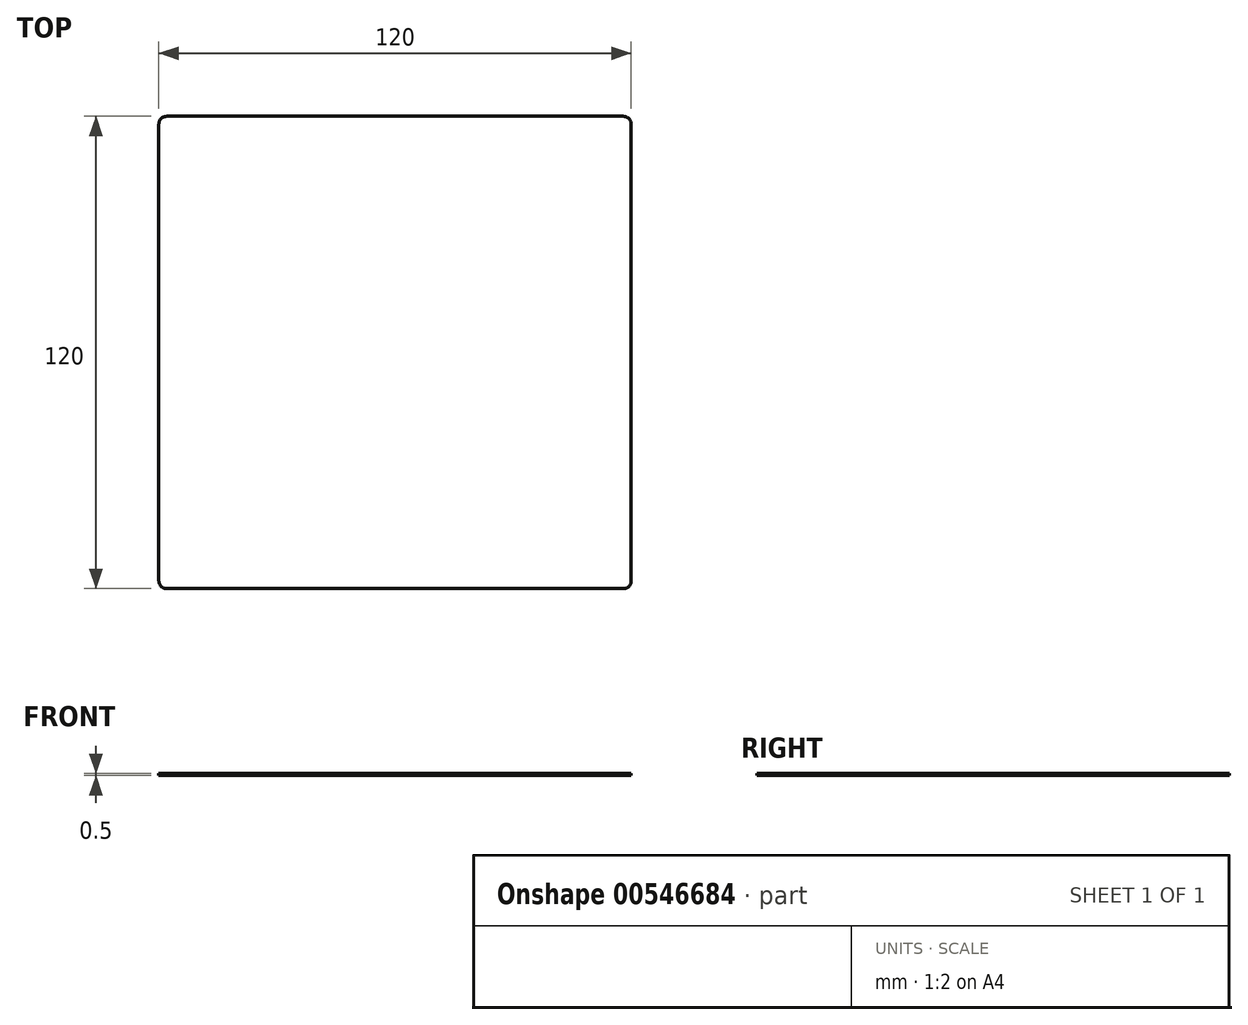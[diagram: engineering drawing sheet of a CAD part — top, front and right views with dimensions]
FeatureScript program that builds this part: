
annotation { "Feature Type Name" : "Feature", "Feature Type Description" : "" }
export const myFeature = defineFeature(function(context is Context, id is Id, definition is map)
    precondition{}
    {
        {
            var Q0;
            Q0=qCreatedBy(makeId("Top.planeOp"),FACE);
            var sketch = newSketch(context, id + "F0", { "sketchPlane" : qUnion([Q0])});
            skLineSegment(sketch, "E0.bottom", {"start": v(-60, -60) * mm, "end": v(60, -60) * mm});
            skLineSegment(sketch, "E0.top", {"start": v(-60, 60) * mm, "end": v(60, 60) * mm});
            skLineSegment(sketch, "E0.left", {"start": v(-60, -60) * mm, "end": v(-60, 60) * mm});
            skLineSegment(sketch, "E0.right", {"start": v(60, -60) * mm, "end": v(60, 60) * mm});
            skPoint(sketch, "E0.middle", {"position": v(0, 0) * mm});
            skSolve(sketch);
        }
        {
            var Q0;
            Q0 = qSketchRegion(id + "F0", true);
            extrude(context, id + "F1", {"entities" : qUnion([Q0]), "depth" : 0.5 * mm, "offsetDistance" : 25 * mm});
        }
        {
            var Q0;
            Q0=makeQuery(id+"F1.opExtrude","SWEPT_EDGE",EDGE,{"disambiguationData":[OSD([sQuery(id+"F0.wireOp",EDGE,"E0.bottom"),sQuery(id+"F0.wireOp",EDGE,"E0.right")])]});
            var Q1;
            Q1=makeQuery(id+"F1.opExtrude","SWEPT_EDGE",EDGE,{"disambiguationData":[OSD([sQuery(id+"F0.wireOp",EDGE,"E0.bottom"),sQuery(id+"F0.wireOp",EDGE,"E0.left")])]});
            var Q2;
            Q2=makeQuery(id+"F1.opExtrude","SWEPT_EDGE",EDGE,{"disambiguationData":[OSD([sQuery(id+"F0.wireOp",EDGE,"E0.top"),sQuery(id+"F0.wireOp",EDGE,"E0.right")])]});
            var Q3;
            Q3=makeQuery(id+"F1.opExtrude","SWEPT_EDGE",EDGE,{"disambiguationData":[OSD([sQuery(id+"F0.wireOp",EDGE,"E0.top"),sQuery(id+"F0.wireOp",EDGE,"E0.left")])]});
            fillet(context, id + "F2", {"entities" : qUnion([Q0, Q1, Q2, Q3]), "radius" : 2 * mm, "tangentPropagation" : true, "allowEdgeOverflow" : false});
        }
    });
